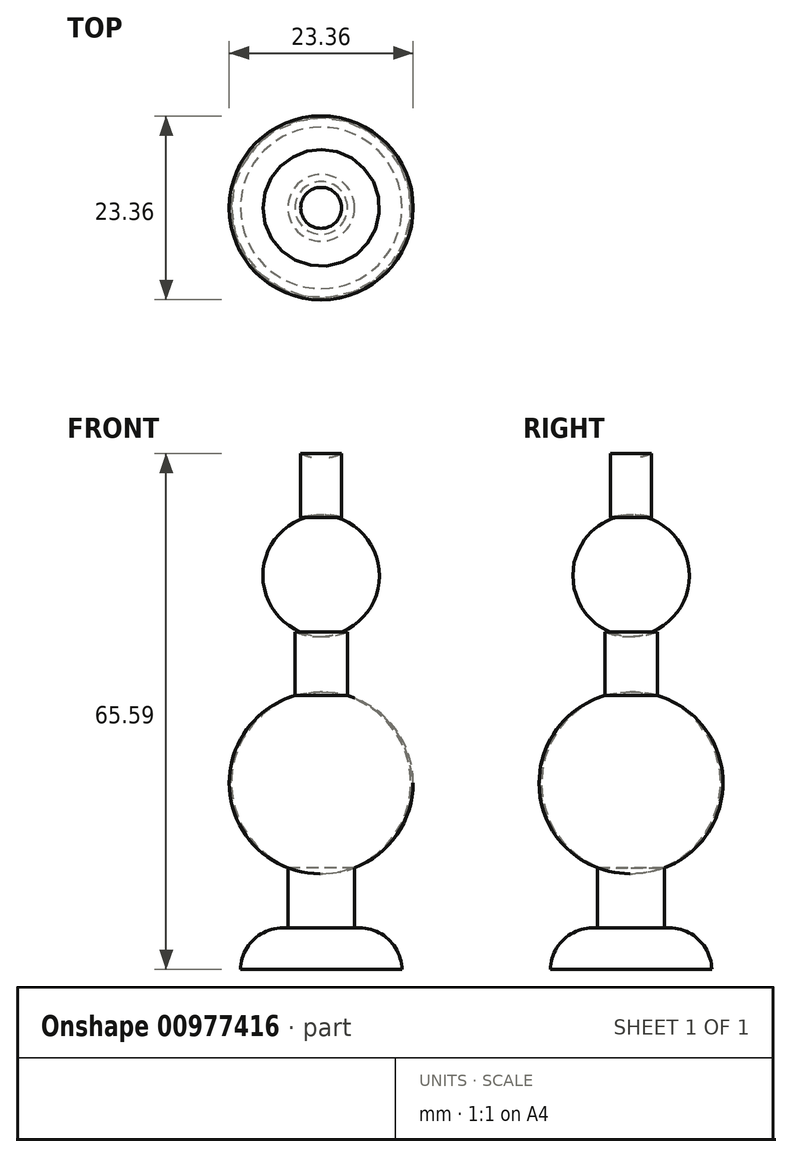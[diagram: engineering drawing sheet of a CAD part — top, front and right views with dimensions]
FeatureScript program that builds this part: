
annotation { "Feature Type Name" : "Feature", "Feature Type Description" : "" }
export const myFeature = defineFeature(function(context is Context, id is Id, definition is map)
    precondition{}
    {
        {
            var Q0;
            Q0=qCreatedBy(makeId("Front.planeOp"),FACE);
            var sketch = newSketch(context, id + "F0", { "sketchPlane" : qUnion([Q0])});
            skLineSegment(sketch, "E0", {"start": v(-4.24, 12.93) * mm, "end": v(-4.24, 5.25) * mm});
            skArc(sketch, "E1", {"start": v(-4.24, 5.25) * mm, "mid": v(-8.42, 3.97) * mm, "end": v(-10.26, 0) * mm});
            skLineSegment(sketch, "E2", {"start": v(-2.6, 65.6) * mm, "end": v(-2.6, 57.44) * mm});
            skLineSegment(sketch, "E3", {"start": v(-3.33, 42.9) * mm, "end": v(-3.33, 34.83) * mm});
            skArc(sketch, "E4", {"start": v(-3.33, 34.83) * mm, "mid": v(-11.48, 24.2) * mm, "end": v(-4.24, 12.93) * mm});
            skArc(sketch, "E5", {"start": v(-2.6, 57.44) * mm, "mid": v(-8.06, 50.43) * mm, "end": v(-3.33, 42.9) * mm});
            skArc(sketch, "E6", {"start": v(0, 73.52) * mm, "mid": v(-4.55, 70.62) * mm, "end": v(-2.6, 65.6) * mm});
            skLineSegment(sketch, "E7", {"start": v(0, 73.52) * mm, "end": v(0, 0) * mm});
            skLineSegment(sketch, "E8", {"start": v(0, 0) * mm, "end": v(-10.26, 0) * mm});
            skCircle(sketch, "E9", {"center": v(0.15, 23.71) * mm, "radius": 11.53 * mm});
            skSolve(sketch);
        }
        {
            var Q0;
            Q0=makeQuery(id+"F0.imprint","IMPRINT",FACE,{"disambiguationData":[TD([[makeQuery(id+"F0.imprint","IMPRINT",EDGE,{"derivedFrom":sQuery(id+"F0.wireOp",EDGE,"E0")}),1.0]])]});
            var Q1;
            Q1=sQuery(id+"F0.wireOp",EDGE,"E7");
            revolve(context, id + "F1", {"surfaceOperationType" : NewSurfaceOperationType.NEW, "entities" : qUnion([Q0]), "axis" : qUnion([Q1]), "revolveType" : RevolveType.FULL});
        }
    });
